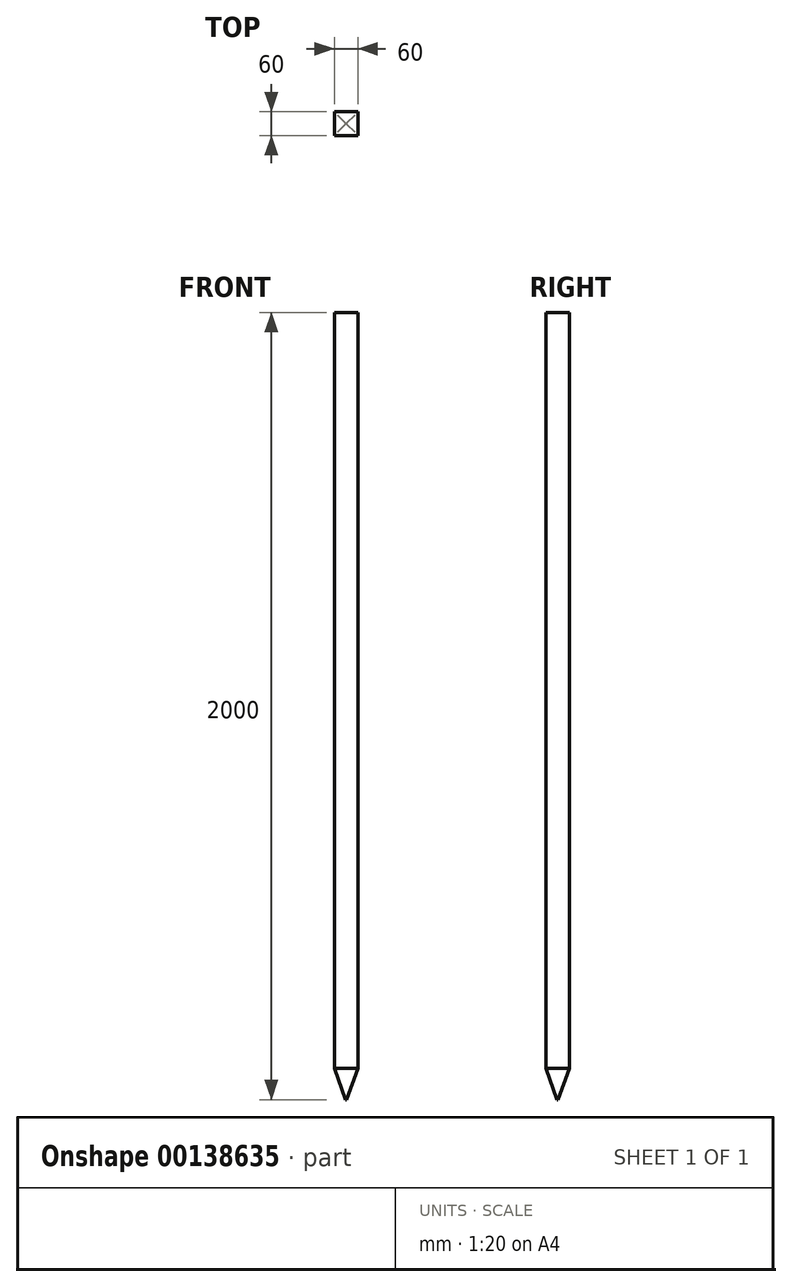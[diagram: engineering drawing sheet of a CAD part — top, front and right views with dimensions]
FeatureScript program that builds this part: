
annotation { "Feature Type Name" : "Feature", "Feature Type Description" : "" }
export const myFeature = defineFeature(function(context is Context, id is Id, definition is map)
    precondition{}
    {
        {
            var Q0;
            Q0=qCreatedBy(makeId("Top.planeOp"),FACE);
            var sketch = newSketch(context, id + "F0", { "sketchPlane" : qUnion([Q0])});
            skLineSegment(sketch, "E0.bottom", {"start": v(30, 30) * mm, "end": v(-30, 30) * mm});
            skLineSegment(sketch, "E0.top", {"start": v(30, -30) * mm, "end": v(-30, -30) * mm});
            skLineSegment(sketch, "E0.left", {"start": v(30, 30) * mm, "end": v(30, -30) * mm});
            skLineSegment(sketch, "E0.right", {"start": v(-30, 30) * mm, "end": v(-30, -30) * mm});
            skPoint(sketch, "E0.middle", {"position": v(0, 0) * mm});
            skSolve(sketch);
        }
        {
            var Q0;
            Q0 = qSketchRegion(id + "F0", true);
            extrude(context, id + "F1", {"entities" : qUnion([Q0]), "oppositeDirection" : true, "depth" : 2000 * mm});
        }
        {
            var Q0;
            Q0=makeQuery(id+"F1.opExtrude","CAP_FACE",FACE,{"disambiguationData":[OSD([sQuery(id+"F0.wireOp",EDGE,"E0.bottom"),sQuery(id+"F0.wireOp",EDGE,"E0.top"),sQuery(id+"F0.wireOp",EDGE,"E0.left"),sQuery(id+"F0.wireOp",EDGE,"E0.right")])],"isStart":false});
            chamfer(context, id + "F2", {"entities" : qUnion([Q0]), "chamferType" : ChamferType.OFFSET_ANGLE, "width" : 80 * mm, "oppositeDirection" : false, "angle" : 20 * degree, "tangentPropagation" : true});
        }
    });
